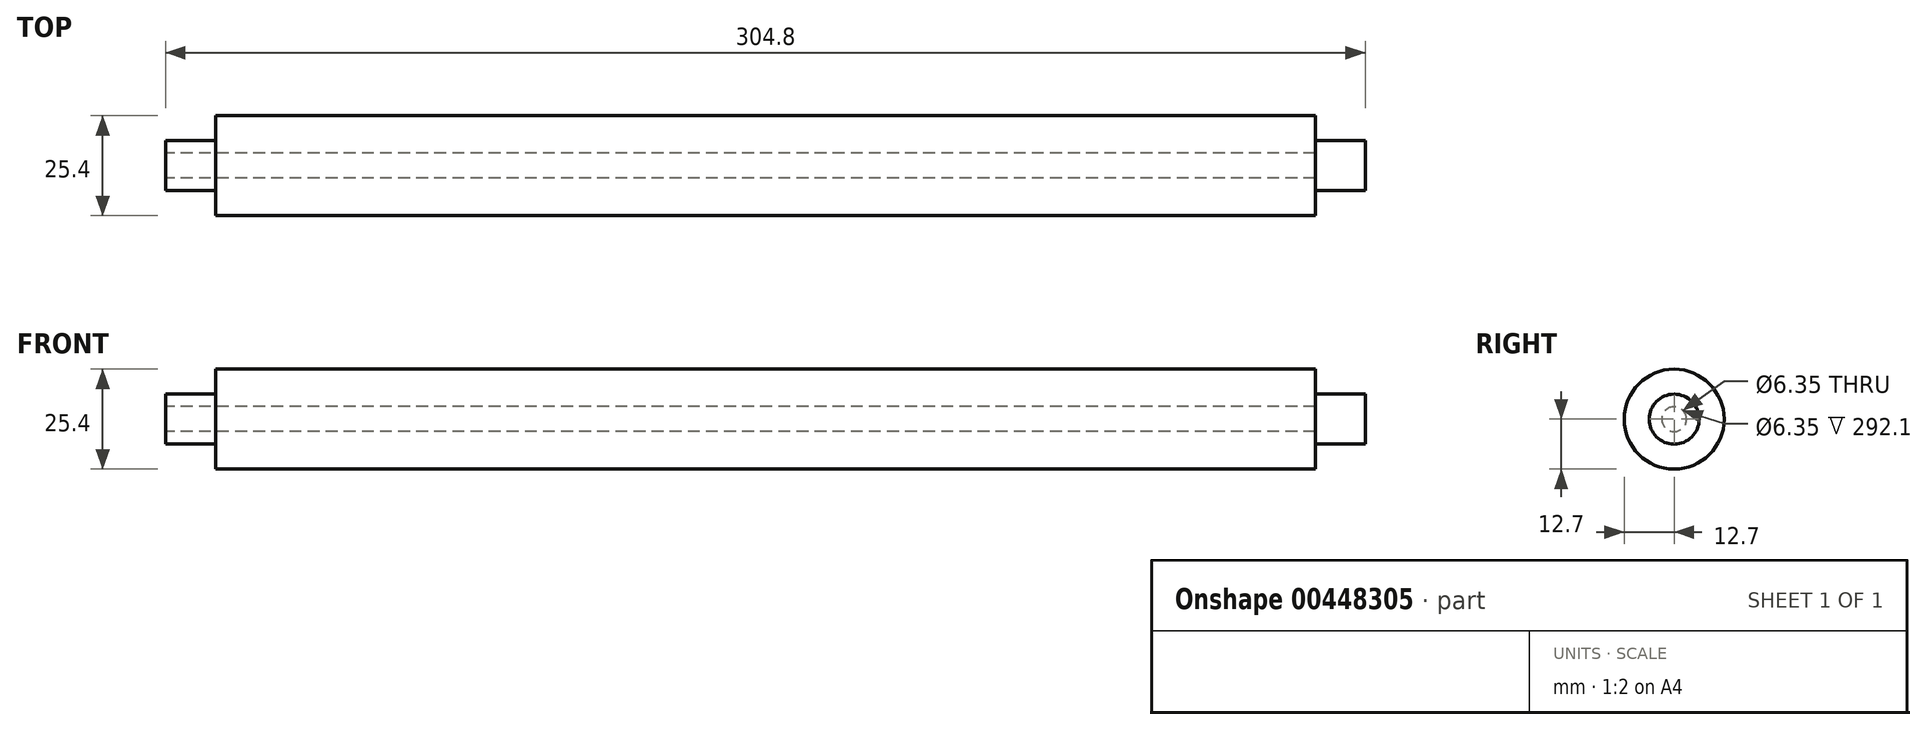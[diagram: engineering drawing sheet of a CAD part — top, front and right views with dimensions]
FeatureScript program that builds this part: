
annotation { "Feature Type Name" : "Feature", "Feature Type Description" : "" }
export const myFeature = defineFeature(function(context is Context, id is Id, definition is map)
    precondition{}
    {
        {
            var Q0;
            Q0=qCreatedBy(makeId("Front.planeOp"),FACE);
            var sketch = newSketch(context, id + "F0", { "sketchPlane" : qUnion([Q0])});
            skLineSegment(sketch, "E0.bottom", {"start": v(139.7, 12.7) * mm, "end": v(-139.7, 12.7) * mm});
            skLineSegment(sketch, "E0.top", {"start": v(139.7, -12.7) * mm, "end": v(-139.7, -12.7) * mm});
            skLineSegment(sketch, "E0.left", {"start": v(139.7, 12.7) * mm, "end": v(139.7, -12.7) * mm});
            skLineSegment(sketch, "E0.right", {"start": v(-139.7, 12.7) * mm, "end": v(-139.7, -12.7) * mm});
            skPoint(sketch, "E0.middle", {"position": v(0, 0) * mm});
            skLineSegment(sketch, "E1", {"start": v(-139.7, 3.17) * mm, "end": v(139.7, 3.18) * mm});
            skLineSegment(sketch, "E2", {"start": v(-139.7, -3.18) * mm, "end": v(139.7, -3.17) * mm});
            skLineSegment(sketch, "E3", {"start": v(139.7, 6.35) * mm, "end": v(152.4, 6.35) * mm});
            skLineSegment(sketch, "E4", {"start": v(152.4, 6.35) * mm, "end": v(152.4, -6.35) * mm});
            skLineSegment(sketch, "E5", {"start": v(152.4, -6.35) * mm, "end": v(139.7, -6.35) * mm});
            skLineSegment(sketch, "E6", {"start": v(-139.7, 6.35) * mm, "end": v(-152.4, 6.35) * mm});
            skLineSegment(sketch, "E7", {"start": v(-152.4, 6.35) * mm, "end": v(-152.4, -6.35) * mm});
            skLineSegment(sketch, "E8", {"start": v(-152.4, -6.35) * mm, "end": v(-139.7, -6.35) * mm});
            skLineSegment(sketch, "E9", {"start": v(-139.7, 3.17) * mm, "end": v(-152.4, 3.17) * mm});
            skLineSegment(sketch, "E10", {"start": v(-152.4, 3.17) * mm, "end": v(-152.4, -3.18) * mm});
            skLineSegment(sketch, "E11", {"start": v(-152.4, -3.18) * mm, "end": v(-139.7, -3.18) * mm});
            skLineSegment(sketch, "E12", {"start": v(-152.4, 0) * mm, "end": v(152.4, 0) * mm});
            skSolve(sketch);
        }
        {
            var Q0;
            {var subQ2=sQuery(id+"F0.wireOp",EDGE,"E6");Q0=makeQuery(id+"F0.imprint","IMPRINT",FACE,{"disambiguationData":[TD([[makeQuery(id+"F0.imprint","IMPRINT",EDGE,{"derivedFrom":subQ2}),1.0]])]});}
            var Q1;
            {var subQ2=sQuery(id+"F0.wireOp",EDGE,"E8");Q1=makeQuery(id+"F0.imprint","IMPRINT",FACE,{"disambiguationData":[TD([[makeQuery(id+"F0.imprint","IMPRINT",EDGE,{"derivedFrom":subQ2}),1.0]])]});}
            var Q2;
            {var subQ1=sQuery(id+"F0.wireOp",EDGE,"E0.bottom");Q2=makeQuery(id+"F0.imprint","IMPRINT",FACE,{"disambiguationData":[TD([[makeQuery(id+"F0.imprint","IMPRINT",EDGE,{"derivedFrom":subQ1}),1.0]])]});}
            var Q3;
            {var subQ3=sQuery(id+"F0.wireOp",EDGE,"E0.top");Q3=makeQuery(id+"F0.imprint","IMPRINT",FACE,{"disambiguationData":[TD([[makeQuery(id+"F0.imprint","IMPRINT",EDGE,{"derivedFrom":subQ3}),-1.0]])]});}
            var Q4;
            {var subQ0=sQuery(id+"F0.wireOp",EDGE,"E5");Q4=makeQuery(id+"F0.imprint","IMPRINT",FACE,{"disambiguationData":[TD([[makeQuery(id+"F0.imprint","IMPRINT",EDGE,{"derivedFrom":subQ0}),-1.0]])]});}
            var Q5;
            Q5=sQuery(id+"F0.wireOp",EDGE,"E12");
            revolve(context, id + "F1", {"entities" : qUnion([Q0, Q1, Q2, Q3, Q4]), "axis" : qUnion([Q5]), "revolveType" : RevolveType.FULL});
        }
    });
